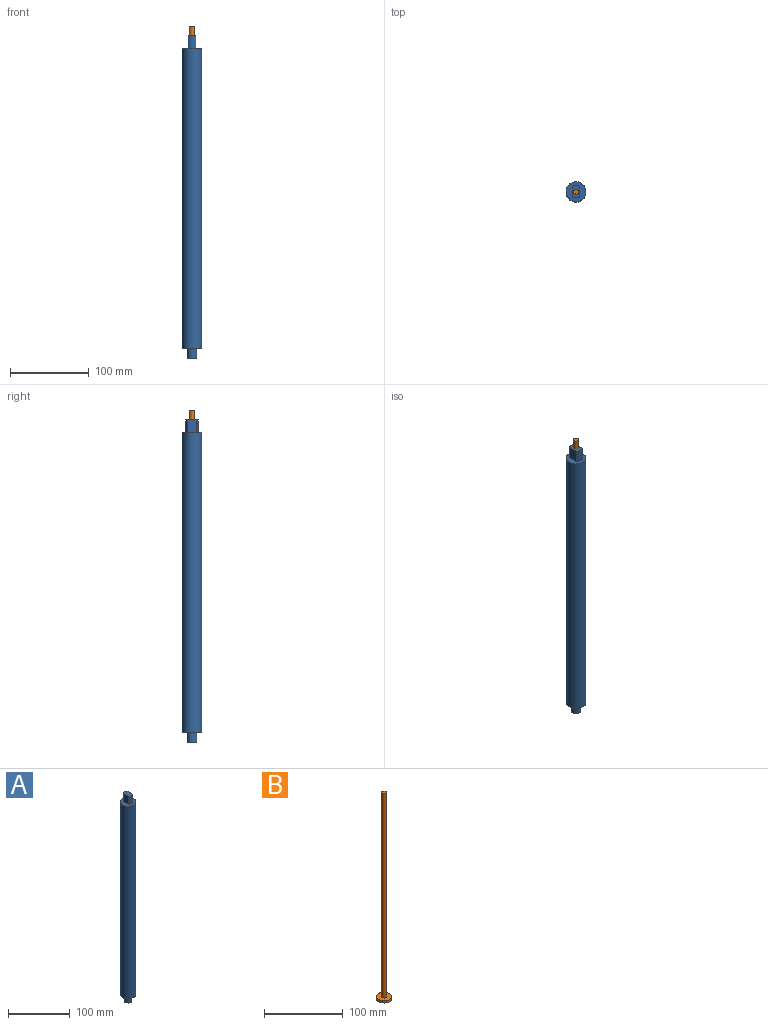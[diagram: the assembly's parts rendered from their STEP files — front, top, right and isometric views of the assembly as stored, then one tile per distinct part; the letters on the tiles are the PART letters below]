
ASSEMBLY  parts=2 mates=1
PART A: 10 faces, bbox 25.4x25.4x409.6 mm
  f0: cylinder r=12.7mm len=381mm, axis (0,0,-1), area 30402.4mm2, adj f1,f2
  f1: plane 25.4x25.4mm, normal (0,0,1), area 365.1mm2, adj f0,f3,f4,f5,f6
  f2: plane 25.4x25.4mm, normal (0,0,-1), area 380mm2, adj f0,f8
  f3: cylinder r=7.94mm len=15.88mm, axis (0,0,-1), area 162.2mm2, adj f1,f4,f6,f7
  f4: plane 15.88x12.7mm, normal (1,0,0), area 201.6mm2, adj f1,f3,f5,f7
  f5: cylinder r=7.94mm len=15.88mm, axis (0,0,-1), area 162.2mm2, adj f1,f4,f6,f7
  f6: plane 15.88x12.7mm, normal (-1,0,0), area 201.6mm2, adj f1,f3,f5,f7
  f7: plane 15.88x9.53mm, normal (0,0,1), area 141.6mm2, adj f3,f4,f5,f6
  f8: cylinder r=6.35mm len=12.7mm, axis (0,0,1), area 506.7mm2, adj f2,f9
  f9: plane 12.7x12.7mm, normal (0,0,-1), area 126.7mm2, adj f8
PART B: 5 faces, bbox 19.1x19.1x320.7 mm
  f0: cylinder r=9.53mm len=19.05mm, axis (0,0,-1), area 190mm2, adj f1,f2
  f1: plane 19.05x19.05mm, normal (0,0,1), area 253.4mm2, adj f0,f3
  f2: plane 19.05x19.05mm, normal (0,0,-1), area 285mm2, adj f0
  f3: cylinder r=3.17mm len=317.5mm, axis (0,0,-1), area 6333.8mm2, adj f1,f4
  f4: plane 6.35x6.35mm, normal (0,0,1), area 31.7mm2, adj f3
PLACE A t=(4.04,4.67,-209.85)mm fixed
PLACE B rot(axis=(0,0,1),0deg) t=(4.04,4.67,-120.95)mm
MATE slider A.f0 <-> B.f0  axis (0,0,-1) through (4.04,4.67,-209.85)mm
